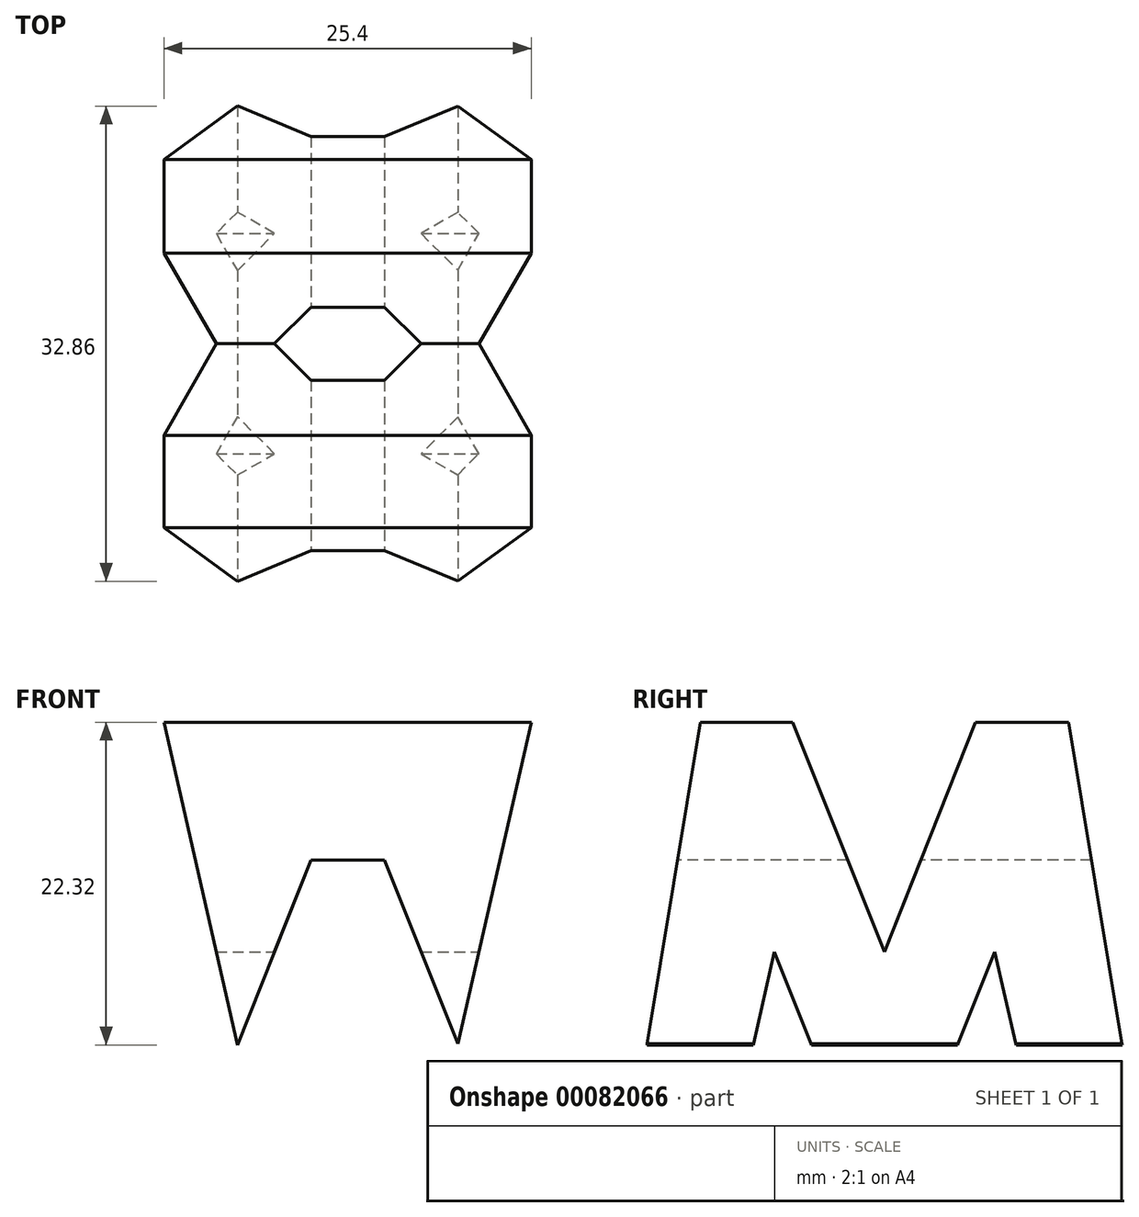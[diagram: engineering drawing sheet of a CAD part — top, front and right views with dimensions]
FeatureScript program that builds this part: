
annotation { "Feature Type Name" : "Feature", "Feature Type Description" : "" }
export const myFeature = defineFeature(function(context is Context, id is Id, definition is map)
    precondition{}
    {
        {
            var Q0;
            Q0=qCreatedBy(makeId("Front.planeOp"),FACE);
            var sketch = newSketch(context, id + "F0", { "sketchPlane" : qUnion([Q0])});
            skLineSegment(sketch, "E0", {"start": v(0, 0) * mm, "end": v(0, 38.1) * mm});
            skLineSegment(sketch, "E1", {"start": v(0, 38.1) * mm, "end": v(38.1, 38.1) * mm});
            skLineSegment(sketch, "E2", {"start": v(38.1, 38.1) * mm, "end": v(38.1, 0) * mm});
            skLineSegment(sketch, "E3", {"start": v(38.1, 0) * mm, "end": v(0, 0) * mm});
            skSolve(sketch);
        }
        {
            var Q0;
            Q0=makeQuery(id+"F0.imprint","IMPRINT",FACE,{"disambiguationData":[TD([[makeQuery(id+"F0.imprint","IMPRINT",EDGE,{"derivedFrom":sQuery(id+"F0.wireOp",EDGE,"E0")}),-1.0]])]});
            extrude(context, id + "F1", {"entities" : qUnion([Q0]), "depth" : 38.1 * mm});
        }
        {
            var Q0;
            Q0=qCreatedBy(makeId("Right.planeOp"),FACE);
            cPlane(context, id + "F2", {"entities" : qUnion([Q0]), "cplaneType" : CPlaneType.OFFSET, "offset" : 38.1 * mm, "width" : 152.4 * mm, "height" : 152.4 * mm});
        }
        {
            var Q0;
            Q0=qCreatedBy(makeId("Front.planeOp"),FACE);
            cPlane(context, id + "F3", {"entities" : qUnion([Q0]), "cplaneType" : CPlaneType.OFFSET, "offset" : 38.1 * mm, "width" : 152.4 * mm, "height" : 152.4 * mm});
        }
        {
            var Q0;
            Q0=qCreatedBy(makeId("Top.planeOp"),FACE);
            cPlane(context, id + "F4", {"entities" : qUnion([Q0]), "cplaneType" : CPlaneType.OFFSET, "offset" : 38.1 * mm, "width" : 152.4 * mm, "height" : 152.4 * mm});
        }
        {
            var Q0;
            Q0=qCreatedBy(id+"F3.planeOp",FACE);
            var sketch = newSketch(context, id + "F5", { "sketchPlane" : qUnion([Q0])});
            skLineSegment(sketch, "E4", {"start": v(0, 0) * mm, "end": v(0, 38.1) * mm});
            skLineSegment(sketch, "E5", {"start": v(0, 38.1) * mm, "end": v(38.1, 38.1) * mm});
            skLineSegment(sketch, "E6", {"start": v(38.1, 0) * mm, "end": v(0, 0) * mm});
            skLineSegment(sketch, "E7", {"start": v(38.1, 0) * mm, "end": v(38.1, 38.1) * mm});
            skLineSegment(sketch, "E8", {"start": v(0, 38.1) * mm, "end": v(6.35, 0) * mm});
            skLineSegment(sketch, "E9", {"start": v(31.75, 0) * mm, "end": v(38.1, 38.1) * mm});
            skLineSegment(sketch, "E10", {"start": v(6.35, 38.1) * mm, "end": v(11.43, 15.78) * mm});
            skLineSegment(sketch, "E11", {"start": v(11.43, 15.78) * mm, "end": v(16.51, 28.57) * mm});
            skLineSegment(sketch, "E12", {"start": v(16.51, 28.58) * mm, "end": v(21.59, 28.58) * mm});
            skLineSegment(sketch, "E13", {"start": v(21.59, 28.57) * mm, "end": v(26.67, 15.88) * mm});
            skLineSegment(sketch, "E14", {"start": v(26.67, 15.88) * mm, "end": v(31.75, 38.1) * mm});
            skPoint(sketch, "E15.startSnap0", {"position": v(13.97, 22.18) * mm});
            skLineSegment(sketch, "E16", {"start": v(12.7, 0) * mm, "end": v(19.05, 15.88) * mm});
            skLineSegment(sketch, "E17", {"start": v(19.05, 15.87) * mm, "end": v(25.4, 0) * mm});
            skLineSegment(sketch, "E18", {"start": v(6.35, 38.1) * mm, "end": v(0, 38.1) * mm});
            skLineSegment(sketch, "E19", {"start": v(31.75, 38.1) * mm, "end": v(38.1, 38.1) * mm});
            skLineSegment(sketch, "E20", {"start": v(0, 38.1) * mm, "end": v(6.35, 38.1) * mm});
            skLineSegment(sketch, "E21", {"start": v(6.35, 0) * mm, "end": v(12.7, 0) * mm});
            skLineSegment(sketch, "E22", {"start": v(25.4, 0) * mm, "end": v(31.75, 0) * mm});
            skLineSegment(sketch, "E23", {"start": v(12.7, 0) * mm, "end": v(12.7, 0) * mm});
            skSolve(sketch);
        }
        {
            var Q0;
            {var subQ0=sQuery(id+"F5.wireOp",EDGE,"E4");Q0=makeQuery(id+"F5.imprint","IMPRINT",FACE,{"disambiguationData":[TD([[makeQuery(id+"F5.imprint","IMPRINT",EDGE,{"derivedFrom":subQ0}),-1.0]])]});}
            var Q1;
            Q1=makeQuery(id+"F5.imprint","IMPRINT",FACE,{"disambiguationData":[TD([[makeQuery(id+"F5.imprint","IMPRINT",EDGE,{"derivedFrom":sQuery(id+"F5.wireOp",EDGE,"E5")}),-1.0]])]});
            var Q2;
            {var subQ0=sQuery(id+"F5.wireOp",EDGE,"E7");Q2=makeQuery(id+"F5.imprint","IMPRINT",FACE,{"disambiguationData":[TD([[makeQuery(id+"F5.imprint","IMPRINT",EDGE,{"derivedFrom":subQ0}),1.0]])]});}
            var Q3;
            {var subQ0=sQuery(id+"F5.wireOp",EDGE,"E16");Q3=makeQuery(id+"F5.imprint","IMPRINT",FACE,{"disambiguationData":[TD([[makeQuery(id+"F5.imprint","IMPRINT",EDGE,{"derivedFrom":subQ0}),-1.0]])]});}
            extrude(context, id + "F6", {"entities" : qUnion([Q0, Q1, Q2, Q3]), "operationType" : NewBodyOperationType.REMOVE, "oppositeDirection" : true, "depth" : 38.1 * mm});
        }
        {
            var Q0;
            Q0=qCreatedBy(id+"F2.planeOp",FACE);
            var sketch = newSketch(context, id + "F7", { "sketchPlane" : qUnion([Q0])});
            skLineSegment(sketch, "E24", {"start": v(-38.1, 0) * mm, "end": v(-31.75, 38.31) * mm});
            skLineSegment(sketch, "E25", {"start": v(-6.35, 38.31) * mm, "end": v(0, 0) * mm});
            skLineSegment(sketch, "E26", {"start": v(-31.75, 0) * mm, "end": v(-26.67, 22.23) * mm});
            skLineSegment(sketch, "E27", {"start": v(-26.67, 22.23) * mm, "end": v(-21.6, 9.53) * mm});
            skLineSegment(sketch, "E28", {"start": v(-21.6, 9.53) * mm, "end": v(-16.51, 9.53) * mm});
            skLineSegment(sketch, "E29", {"start": v(-16.51, 9.53) * mm, "end": v(-11.43, 22.23) * mm});
            skLineSegment(sketch, "E30", {"start": v(-11.43, 22.23) * mm, "end": v(-6.35, 0) * mm});
            skLineSegment(sketch, "E31", {"start": v(-25.4, 38.1) * mm, "end": v(-19.05, 22.23) * mm});
            skLineSegment(sketch, "E32", {"start": v(-19.05, 22.23) * mm, "end": v(-12.7, 38.3) * mm});
            skLineSegment(sketch, "E33", {"start": v(0, 38.1) * mm, "end": v(0, 0) * mm});
            skLineSegment(sketch, "E34", {"start": v(-38.1, 38.1) * mm, "end": v(0, 38.1) * mm});
            skLineSegment(sketch, "E35", {"start": v(-38.1, 38.1) * mm, "end": v(-38.1, 0) * mm});
            skLineSegment(sketch, "E36", {"start": v(-38.1, 0) * mm, "end": v(0, 0) * mm});
            skSolve(sketch);
        }
        {
            var Q0;
            {var subQ0=sQuery(id+"F7.wireOp",EDGE,"E35");Q0=makeQuery(id+"F7.imprint","IMPRINT",FACE,{"disambiguationData":[TD([[makeQuery(id+"F7.imprint","IMPRINT",EDGE,{"derivedFrom":subQ0}),1.0]])]});}
            var Q1;
            {var subQ0=sQuery(id+"F7.wireOp",EDGE,"E26");Q1=makeQuery(id+"F7.imprint","IMPRINT",FACE,{"disambiguationData":[TD([[makeQuery(id+"F7.imprint","IMPRINT",EDGE,{"derivedFrom":subQ0}),-1.0]])]});}
            var Q2;
            {var subQ0=sQuery(id+"F7.wireOp",EDGE,"E31");Q2=makeQuery(id+"F7.imprint","IMPRINT",FACE,{"disambiguationData":[TD([[makeQuery(id+"F7.imprint","IMPRINT",EDGE,{"derivedFrom":subQ0}),1.0]])]});}
            var Q3;
            {var subQ0=sQuery(id+"F7.wireOp",EDGE,"E33");Q3=makeQuery(id+"F7.imprint","IMPRINT",FACE,{"disambiguationData":[TD([[makeQuery(id+"F7.imprint","IMPRINT",EDGE,{"derivedFrom":subQ0}),-1.0]])]});}
            extrude(context, id + "F8", {"entities" : qUnion([Q0, Q1, Q2, Q3]), "operationType" : NewBodyOperationType.REMOVE, "oppositeDirection" : true, "depth" : 38.1 * mm});
        }
    });
